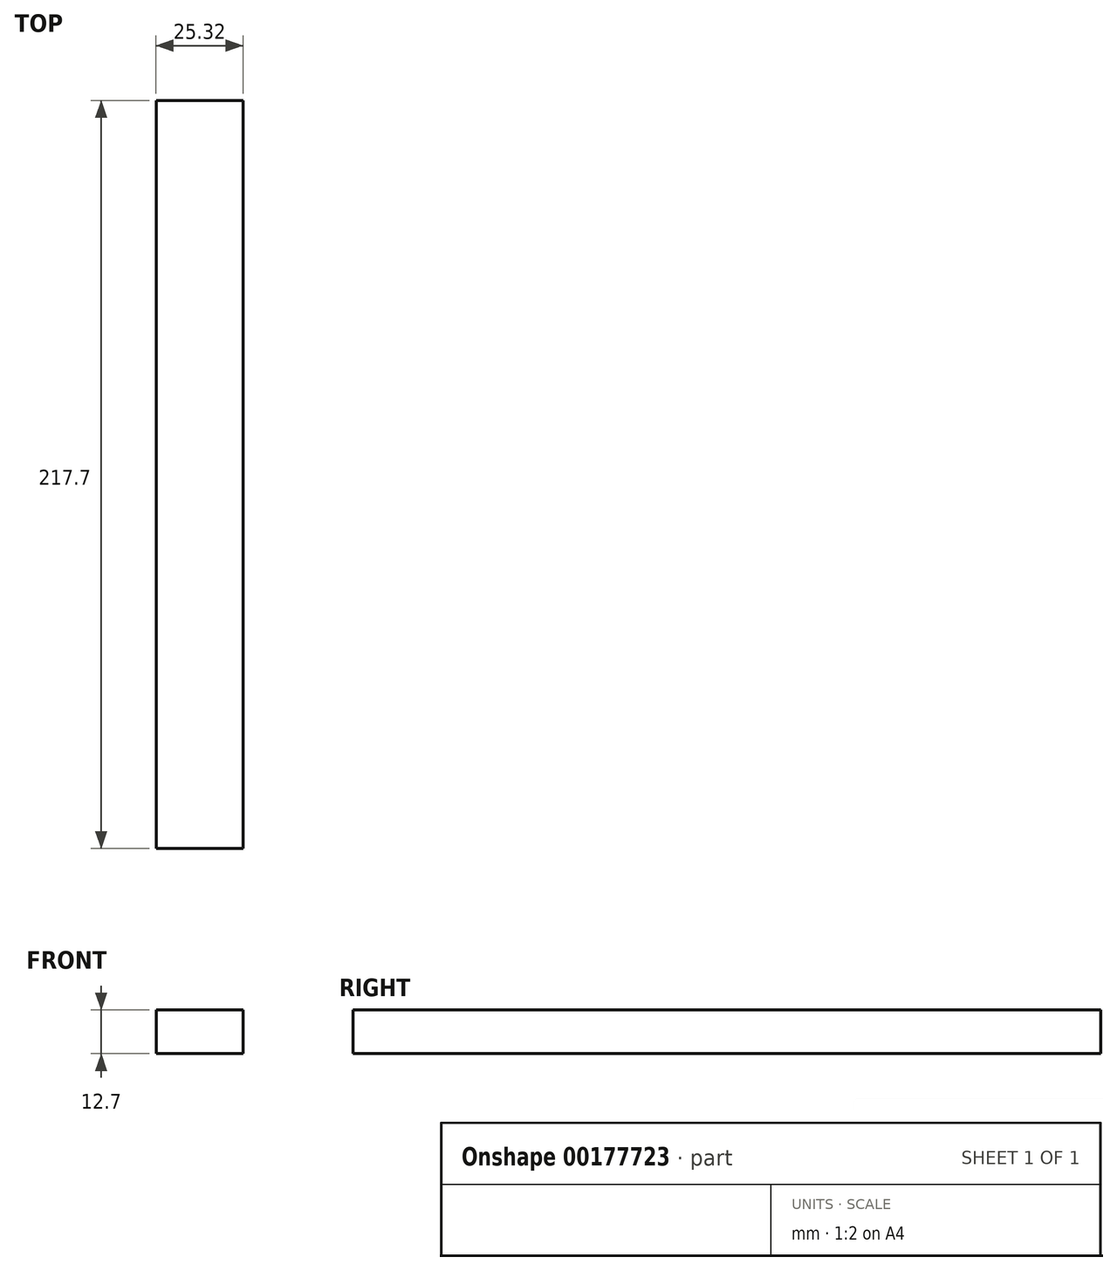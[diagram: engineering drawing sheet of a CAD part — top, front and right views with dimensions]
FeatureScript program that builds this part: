
annotation { "Feature Type Name" : "Feature", "Feature Type Description" : "" }
export const myFeature = defineFeature(function(context is Context, id is Id, definition is map)
    precondition{}
    {
        {
            var Q0;
            Q0=qCreatedBy(makeId("Top.planeOp"),FACE);
            var sketch = newSketch(context, id + "F0", { "sketchPlane" : qUnion([Q0])});
            skLineSegment(sketch, "E0.bottom", {"start": v(12.66, 108.85) * mm, "end": v(-12.66, 108.85) * mm});
            skLineSegment(sketch, "E0.top", {"start": v(12.66, -108.85) * mm, "end": v(-12.66, -108.85) * mm});
            skLineSegment(sketch, "E0.left", {"start": v(12.66, 108.85) * mm, "end": v(12.66, -108.85) * mm});
            skLineSegment(sketch, "E0.right", {"start": v(-12.66, 108.85) * mm, "end": v(-12.66, -108.85) * mm});
            skPoint(sketch, "E0.middle", {"position": v(0, 0) * mm});
            skSolve(sketch);
        }
        {
            var Q0;
            Q0=makeQuery(id+"F0.imprint","IMPRINT",FACE,{"disambiguationData":[TD([[makeQuery(id+"F0.imprint","IMPRINT",EDGE,{"derivedFrom":sQuery(id+"F0.wireOp",EDGE,"E0.bottom")}),1.0]])]});
            extrude(context, id + "F1", {"entities" : qUnion([Q0]), "depth" : 12.7 * mm});
        }
    });
